# Revit family: ALKAR-LED_IP65_5W_RECOUVRABLE_BLANC_4000K
name_source: partatom
category: Lighting Fixtures
units: mm (PartAtom-declared; Revit-internal decimal feet)

## family parameters
Always vertical = Yes
Cut with Voids When Loaded = No
Host = Ceiling
Light Source = Yes
OmniClass Number = 23.80.70.11
OmniClass Title = Luminaries for Internal Lighting
Part Type = Normal
Room Calculation Point = No
Round Connector Dimension = Use Diameter
Shared = No

## types (1)
- Type 1
    Alimentation Driver = AC 220-240V
    Alimentation luminaire = ...mA / ...-...V
    Angle d'éclairage = 60°
    Color Filter = 16777215
    Default Elevation = 0 mm  [stored 0 ft]
    Dimensions = ø80 mm; H : 53 mm
    Dimensions d’encastrement = ø60 mm
    Dimming Lamp Color Temperature Shift = <None>
    Driver = Driver intégré No flicker dimmable
    Durée de vie = 50 000 heures
    Fintion = Blanc brillant
    IRC = >80
    Manufacturer = Lucera - Lucera (c) 06/01/2021 16:40:17 +01:00
    Photometric Web File = google_eulumdat_converter.ies
    Puissance nominale = 5W
    SDCM = <4
    Tilt Angle = 90.00°
    Type de lampe = LED Lumileds SMD
    URL = https://www.lucera.fr

note: [stored X ft] marks values corroborated as IEEE doubles in the binary element streams (Revit-internal decimal feet)

## geometry (parser evidence)
native form markers: Sweep x2
no freeform markers — native parametric forms only
